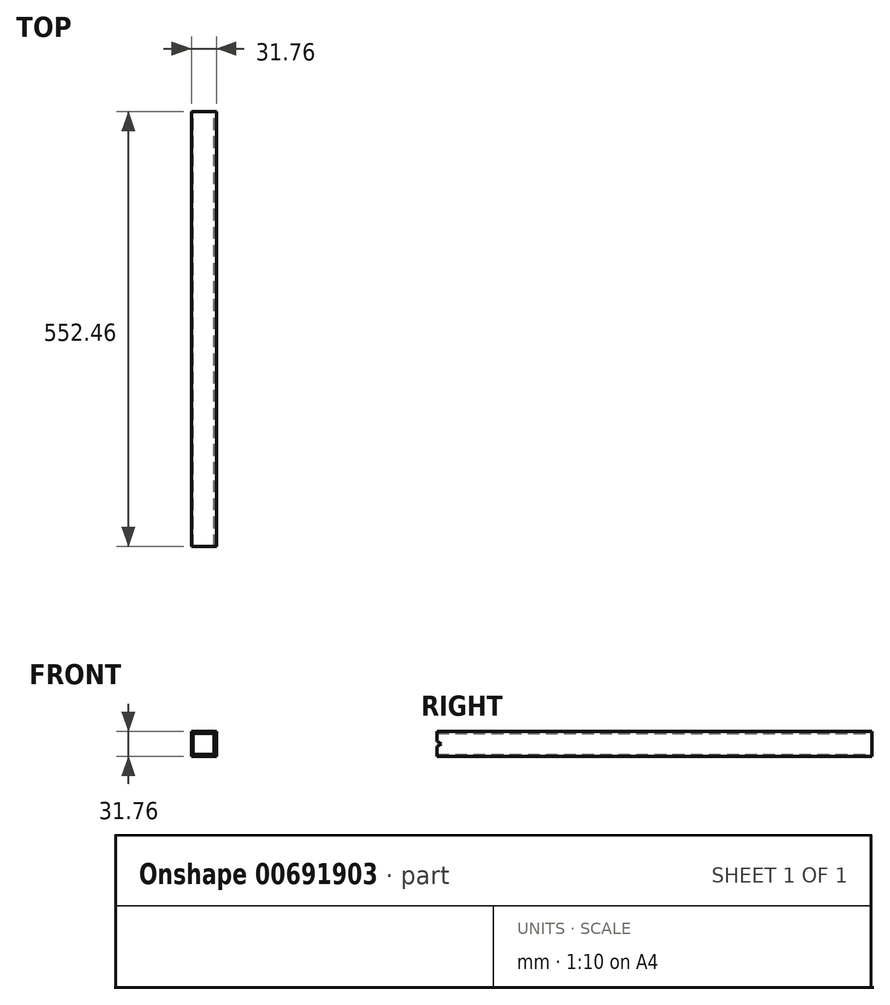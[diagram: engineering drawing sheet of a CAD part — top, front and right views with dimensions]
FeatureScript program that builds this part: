
annotation { "Feature Type Name" : "Feature", "Feature Type Description" : "" }
export const myFeature = defineFeature(function(context is Context, id is Id, definition is map)
    precondition{}
    {
        {
            var Q0;
            Q0=qCreatedBy(makeId("Front.planeOp"),FACE);
            var sketch = newSketch(context, id + "F0", { "sketchPlane" : qUnion([Q0])});
            skLineSegment(sketch, "E0.bottom", {"start": v(15.88, -15.88) * mm, "end": v(-15.88, -15.88) * mm});
            skLineSegment(sketch, "E0.top", {"start": v(15.88, 15.88) * mm, "end": v(-15.87, 15.87) * mm});
            skLineSegment(sketch, "E0.left", {"start": v(15.88, -15.88) * mm, "end": v(15.88, 15.88) * mm});
            skLineSegment(sketch, "E0.right", {"start": v(-15.88, -15.88) * mm, "end": v(-15.88, 15.88) * mm});
            skPoint(sketch, "E0.middle", {"position": v(0, 0) * mm});
            skLineSegment(sketch, "E1.bottom", {"start": v(13.33, -13.34) * mm, "end": v(-13.33, -13.34) * mm});
            skLineSegment(sketch, "E1.top", {"start": v(13.33, 13.34) * mm, "end": v(-13.33, 13.34) * mm});
            skLineSegment(sketch, "E1.left", {"start": v(13.33, -13.34) * mm, "end": v(13.33, 13.33) * mm});
            skLineSegment(sketch, "E1.right", {"start": v(-13.33, -13.34) * mm, "end": v(-13.33, 13.34) * mm});
            skSolve(sketch);
        }
        {
            var Q0;
            Q0=makeQuery(id+"F0.imprint","IMPRINT",FACE,{"disambiguationData":[TD([[makeQuery(id+"F0.imprint","IMPRINT",EDGE,{"derivedFrom":sQuery(id+"F0.wireOp",EDGE,"E0.bottom")}),-1.0]])]});
            extrude(context, id + "F1", {"entities" : qUnion([Q0]), "endBound" : BoundingType.SYMMETRIC, "depth" : 552.45 * mm, "offsetDistance" : 25.4 * mm});
        }
        {
            var Q0;
            Q0=makeQuery(id+"F1.opExtrude","SWEPT_FACE",FACE,{"disambiguationData":[OSD([sQuery(id+"F0.wireOp",EDGE,"E0.left")])]});
            var sketch = newSketch(context, id + "F2", { "sketchPlane" : qUnion([Q0])});
            skLineSegment(sketch, "E2", {"start": v(-270.73, 0) * mm, "end": v(-276.23, 3.18) * mm});
            skLineSegment(sketch, "E3", {"start": v(-270.73, 0) * mm, "end": v(-276.23, -3.18) * mm});
            skLineSegment(sketch, "E4", {"start": v(-276.23, 3.17) * mm, "end": v(-276.23, -3.18) * mm});
            skSolve(sketch);
        }
        {
            var Q0;
            Q0=makeQuery(id+"F2.imprint","IMPRINT",FACE,{"disambiguationData":[TD([[makeQuery(id+"F2.imprint","IMPRINT",EDGE,{"derivedFrom":sQuery(id+"F2.wireOp",EDGE,"E2")}),1.0]])]});
            var Q1;
            Q1=makeQuery(id+"F1.opExtrude","SWEPT_FACE",FACE,{"disambiguationData":[OSD([sQuery(id+"F0.wireOp",EDGE,"E0.right")])]});
            extrude(context, id + "F3", {"entities" : qUnion([Q0]), "operationType" : NewBodyOperationType.REMOVE, "endBound" : BoundingType.UP_TO_SURFACE, "oppositeDirection" : true, "depth" : 25.4 * mm, "endBoundEntityFace" : qUnion([Q1]), "offsetDistance" : 25.4 * mm});
        }
    });
